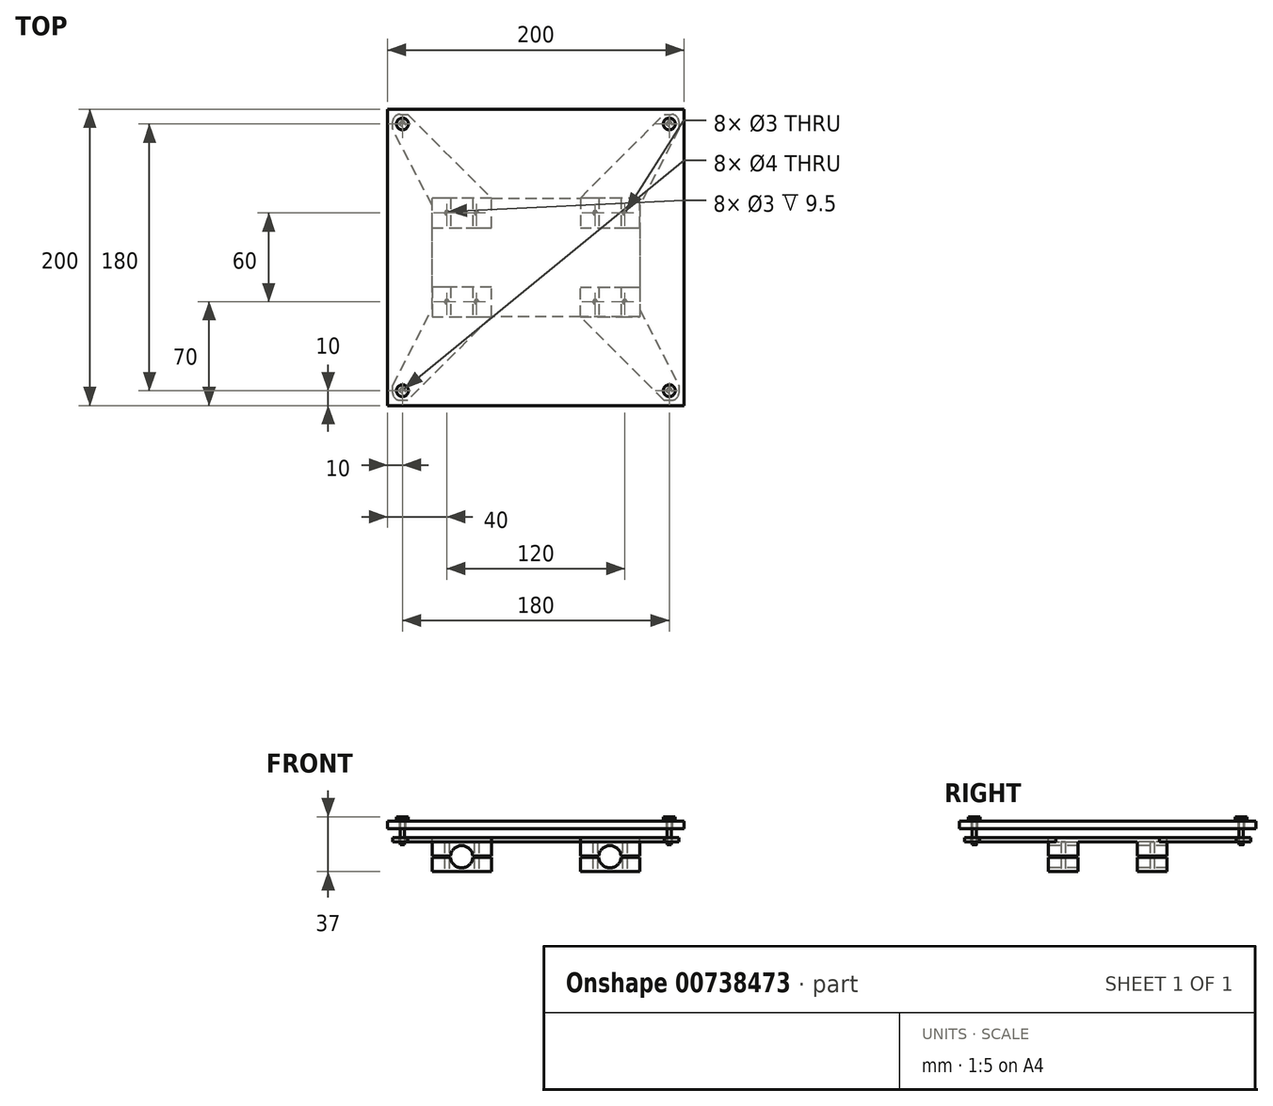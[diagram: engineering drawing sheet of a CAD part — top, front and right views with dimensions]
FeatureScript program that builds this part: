
annotation { "Feature Type Name" : "Feature", "Feature Type Description" : "" }
export const myFeature = defineFeature(function(context is Context, id is Id, definition is map)
    precondition{}
    {
        {
            var Q0;
            Q0=qCreatedBy(makeId("Top.planeOp"),FACE);
            var sketch = newSketch(context, id + "F0", { "sketchPlane" : qUnion([Q0])});
            skLineSegment(sketch, "E0.bottom", {"start": v(100, 100) * mm, "end": v(-100, 100) * mm});
            skLineSegment(sketch, "E0.top", {"start": v(100, -100) * mm, "end": v(-100, -100) * mm});
            skLineSegment(sketch, "E0.left", {"start": v(100, 100) * mm, "end": v(100, -100) * mm});
            skLineSegment(sketch, "E0.right", {"start": v(-100, 100) * mm, "end": v(-100, -100) * mm});
            skPoint(sketch, "E0.middle", {"position": v(0, 0) * mm});
            skLineSegment(sketch, "E1", {"start": v(-90, 100) * mm, "end": v(-90, -100) * mm, "construction": true});
            skLineSegment(sketch, "E2", {"start": v(-90, -100) * mm, "end": v(-100, -90) * mm, "construction": true});
            skLineSegment(sketch, "E3", {"start": v(-100, -90) * mm, "end": v(100, -90) * mm, "construction": true});
            skLineSegment(sketch, "E4", {"start": v(100, -90) * mm, "end": v(90, -100) * mm, "construction": true});
            skLineSegment(sketch, "E5", {"start": v(90, -100) * mm, "end": v(90, 100) * mm, "construction": true});
            skLineSegment(sketch, "E6", {"start": v(90, 100) * mm, "end": v(100, 90) * mm, "construction": true});
            skLineSegment(sketch, "E7", {"start": v(100, 90) * mm, "end": v(-100, 90) * mm, "construction": true});
            skLineSegment(sketch, "E8", {"start": v(-100, 90) * mm, "end": v(-90, 100) * mm, "construction": true});
            skCircle(sketch, "E9", {"center": v(-90, 90) * mm, "radius": 2 * mm});
            skCircle(sketch, "E10", {"center": v(90, 90) * mm, "radius": 2 * mm});
            skCircle(sketch, "E11", {"center": v(90, -90) * mm, "radius": 2 * mm});
            skCircle(sketch, "E12", {"center": v(-90, -90) * mm, "radius": 2 * mm});
            skCircle(sketch, "E13", {"center": v(-90, -90) * mm, "radius": 1.5 * mm});
            skCircle(sketch, "E14", {"center": v(-90, 90) * mm, "radius": 1.5 * mm});
            skCircle(sketch, "E15", {"center": v(90, 90) * mm, "radius": 1.5 * mm});
            skCircle(sketch, "E16", {"center": v(90, -90) * mm, "radius": 1.5 * mm});
            skSolve(sketch);
        }
        {
            var Q0;
            Q0=makeQuery(id+"F0.imprint","IMPRINT",FACE,{"disambiguationData":[TD([[makeQuery(id+"F0.imprint","IMPRINT",EDGE,{"derivedFrom":sQuery(id+"F0.wireOp",EDGE,"E0.bottom")}),1.0]])]});
            extrude(context, id + "F1", {"entities" : qUnion([Q0]), "depth" : 5 * mm, "offsetDistance" : 25 * mm});
        }
        {
            var Q0;
            Q0=makeQuery(id+"F0.imprint","IMPRINT",FACE,{"disambiguationData":[TD([[makeQuery(id+"F0.imprint","IMPRINT",EDGE,{"derivedFrom":sQuery(id+"F0.wireOp",EDGE,"E14")}),1.0]])]});
            var Q1;
            Q1=makeQuery(id+"F0.imprint","IMPRINT",FACE,{"disambiguationData":[TD([[makeQuery(id+"F0.imprint","IMPRINT",EDGE,{"derivedFrom":sQuery(id+"F0.wireOp",EDGE,"E16")}),1.0]])]});
            var Q2;
            Q2=makeQuery(id+"F0.imprint","IMPRINT",FACE,{"disambiguationData":[TD([[makeQuery(id+"F0.imprint","IMPRINT",EDGE,{"derivedFrom":sQuery(id+"F0.wireOp",EDGE,"E13")}),1.0]])]});
            var Q3;
            Q3=makeQuery(id+"F0.imprint","IMPRINT",FACE,{"disambiguationData":[TD([[makeQuery(id+"F0.imprint","IMPRINT",EDGE,{"derivedFrom":sQuery(id+"F0.wireOp",EDGE,"E15")}),1.0]])]});
            extrude(context, id + "F2", {"entities" : qUnion([Q0, Q1, Q2, Q3]), "endBound" : BoundingType.SYMMETRIC, "depth" : 12 * mm, "offsetDistance" : 25 * mm});
        }
        {
            var Q0;
            Q0=makeQuery(id+"F2.opExtrude","CAP_FACE",FACE,{"disambiguationData":[OSD([sQuery(id+"F0.wireOp",EDGE,"E16")])],"isStart":false});
            var sketch = newSketch(context, id + "F3", { "sketchPlane" : qUnion([Q0])});
            skCircle(sketch, "E17", {"center": v(90, -90) * mm, "radius": 4 * mm});
            skSolve(sketch);
        }
        {
            var Q0;
            Q0=makeQuery(id+"F3.imprint","IMPRINT",FACE,{"disambiguationData":[TD([[makeQuery(id+"F3.imprint","IMPRINT",EDGE,{"derivedFrom":sQuery(id+"F3.wireOp",EDGE,"E17")}),1.0]])]});
            var Q1;
            Q1=makeQuery(id+"F3.imprint","IMPRINT",FACE,{"disambiguationData":[TD([[makeQuery(id+"F3.imprint","IMPRINT",EDGE,{"derivedFrom":makeQuery(id+"F2.opExtrude","CAP_EDGE",EDGE,{"disambiguationData":[OSD([sQuery(id+"F0.wireOp",EDGE,"E16")])],"isStart":false})}),1.0]])]});
            extrude(context, id + "F4", {"entities" : qUnion([Q0, Q1]), "operationType" : NewBodyOperationType.ADD, "depth" : 2 * mm, "offsetDistance" : 25 * mm});
        }
        {
            var Q0;
            Q0=makeQuery(id+"F2.opExtrude","CAP_FACE",FACE,{"disambiguationData":[OSD([sQuery(id+"F0.wireOp",EDGE,"E13")])],"isStart":false});
            var sketch = newSketch(context, id + "F5", { "sketchPlane" : qUnion([Q0])});
            skCircle(sketch, "E18", {"center": v(-90, -90) * mm, "radius": 4 * mm});
            skSolve(sketch);
        }
        {
            var Q0;
            Q0=makeQuery(id+"F5.imprint","IMPRINT",FACE,{"disambiguationData":[TD([[makeQuery(id+"F5.imprint","IMPRINT",EDGE,{"derivedFrom":sQuery(id+"F5.wireOp",EDGE,"E18")}),1.0]])]});
            var Q1;
            Q1=makeQuery(id+"F5.imprint","IMPRINT",FACE,{"disambiguationData":[TD([[makeQuery(id+"F5.imprint","IMPRINT",EDGE,{"derivedFrom":makeQuery(id+"F2.opExtrude","CAP_EDGE",EDGE,{"disambiguationData":[OSD([sQuery(id+"F0.wireOp",EDGE,"E13")])],"isStart":false})}),1.0]])]});
            extrude(context, id + "F6", {"entities" : qUnion([Q0, Q1]), "operationType" : NewBodyOperationType.ADD, "depth" : 2 * mm, "offsetDistance" : 25 * mm});
        }
        {
            var Q0;
            Q0=makeQuery(id+"F2.opExtrude","CAP_FACE",FACE,{"disambiguationData":[OSD([sQuery(id+"F0.wireOp",EDGE,"E14")])],"isStart":false});
            var sketch = newSketch(context, id + "F7", { "sketchPlane" : qUnion([Q0])});
            skCircle(sketch, "E19", {"center": v(-90, 90) * mm, "radius": 4 * mm});
            skSolve(sketch);
        }
        {
            var Q0;
            Q0=makeQuery(id+"F7.imprint","IMPRINT",FACE,{"disambiguationData":[TD([[makeQuery(id+"F7.imprint","IMPRINT",EDGE,{"derivedFrom":sQuery(id+"F7.wireOp",EDGE,"E19")}),1.0]])]});
            var Q1;
            Q1=makeQuery(id+"F7.imprint","IMPRINT",FACE,{"disambiguationData":[TD([[makeQuery(id+"F7.imprint","IMPRINT",EDGE,{"derivedFrom":makeQuery(id+"F2.opExtrude","CAP_EDGE",EDGE,{"disambiguationData":[OSD([sQuery(id+"F0.wireOp",EDGE,"E14")])],"isStart":false})}),1.0]])]});
            extrude(context, id + "F8", {"entities" : qUnion([Q0, Q1]), "depth" : 2 * mm, "offsetDistance" : 25 * mm});
        }
        {
            var Q0;
            Q0=makeQuery(id+"F2.opExtrude","CAP_FACE",FACE,{"disambiguationData":[OSD([sQuery(id+"F0.wireOp",EDGE,"E15")])],"isStart":false});
            var sketch = newSketch(context, id + "F9", { "sketchPlane" : qUnion([Q0])});
            skCircle(sketch, "E20", {"center": v(90, 90) * mm, "radius": 4 * mm});
            skSolve(sketch);
        }
        {
            var Q0;
            Q0=makeQuery(id+"F9.imprint","IMPRINT",FACE,{"disambiguationData":[TD([[makeQuery(id+"F9.imprint","IMPRINT",EDGE,{"derivedFrom":sQuery(id+"F9.wireOp",EDGE,"E20")}),1.0]])]});
            var Q1;
            Q1=makeQuery(id+"F9.imprint","IMPRINT",FACE,{"disambiguationData":[TD([[makeQuery(id+"F9.imprint","IMPRINT",EDGE,{"derivedFrom":makeQuery(id+"F2.opExtrude","CAP_EDGE",EDGE,{"disambiguationData":[OSD([sQuery(id+"F0.wireOp",EDGE,"E15")])],"isStart":false})}),1.0]])]});
            extrude(context, id + "F10", {"entities" : qUnion([Q0, Q1]), "operationType" : NewBodyOperationType.ADD, "depth" : 2 * mm, "offsetDistance" : 25 * mm});
        }
        {
            var Q0;
            Q0=makeQuery(id+"F2.opExtrude","CAP_FACE",FACE,{"disambiguationData":[OSD([sQuery(id+"F0.wireOp",EDGE,"E16")])],"isStart":true});
            var sketch = newSketch(context, id + "F11", { "sketchPlane" : qUnion([Q0])});
            skLineSegment(sketch, "E21", {"start": v(-96.5, 96.5) * mm, "end": v(-96.5, 86.5) * mm});
            skLineSegment(sketch, "E22", {"start": v(-96.5, 86.5) * mm, "end": v(-70, 35) * mm});
            skLineSegment(sketch, "E23", {"start": v(-70, 35) * mm, "end": v(-70, -35) * mm});
            skLineSegment(sketch, "E24", {"start": v(-70, -35) * mm, "end": v(-96.5, -86.5) * mm});
            skLineSegment(sketch, "E25", {"start": v(-96.5, -86.5) * mm, "end": v(-96.5, -96.5) * mm});
            skLineSegment(sketch, "E26", {"start": v(-96.5, -96.5) * mm, "end": v(-86.5, -96.5) * mm});
            skLineSegment(sketch, "E27", {"start": v(-86.5, -96.5) * mm, "end": v(-30, -40) * mm});
            skLineSegment(sketch, "E28", {"start": v(-30, -40) * mm, "end": v(30, -40) * mm});
            skLineSegment(sketch, "E29", {"start": v(30, -40) * mm, "end": v(86.5, -96.5) * mm});
            skLineSegment(sketch, "E30", {"start": v(86.5, -96.5) * mm, "end": v(96.5, -96.5) * mm});
            skLineSegment(sketch, "E31", {"start": v(96.5, -96.5) * mm, "end": v(96.5, -86.5) * mm});
            skLineSegment(sketch, "E32", {"start": v(96.5, -86.5) * mm, "end": v(70, -35) * mm});
            skLineSegment(sketch, "E33", {"start": v(70, -35) * mm, "end": v(70, 35) * mm});
            skLineSegment(sketch, "E34", {"start": v(70, 35) * mm, "end": v(96.5, 86.5) * mm});
            skLineSegment(sketch, "E35", {"start": v(96.5, 86.5) * mm, "end": v(96.5, 96.5) * mm});
            skLineSegment(sketch, "E36", {"start": v(96.5, 96.5) * mm, "end": v(86.5, 96.5) * mm});
            skLineSegment(sketch, "E37", {"start": v(86.5, 96.5) * mm, "end": v(30, 40) * mm});
            skLineSegment(sketch, "E38", {"start": v(30, 40) * mm, "end": v(-30, 40) * mm});
            skLineSegment(sketch, "E39", {"start": v(-30, 40) * mm, "end": v(-86.5, 96.5) * mm});
            skLineSegment(sketch, "E40", {"start": v(-86.5, 96.5) * mm, "end": v(-96.5, 96.5) * mm});
            skCircle(sketch, "E41", {"center": v(90, 90) * mm, "radius": 2 * mm});
            skCircle(sketch, "E42", {"center": v(-90, 90) * mm, "radius": 2 * mm});
            skCircle(sketch, "E43", {"center": v(-90, -90) * mm, "radius": 2 * mm});
            skCircle(sketch, "E44", {"center": v(90, -90) * mm, "radius": 2 * mm});
            skSolve(sketch);
        }
        {
            var Q0;
            Q0=makeQuery(id+"F11.imprint","IMPRINT",FACE,{"disambiguationData":[TD([[makeQuery(id+"F11.imprint","IMPRINT",EDGE,{"derivedFrom":sQuery(id+"F11.wireOp",EDGE,"E21")}),1.0]])]});
            extrude(context, id + "F12", {"entities" : qUnion([Q0]), "depth" : 3 * mm, "offsetDistance" : 25 * mm});
        }
        {
            var Q0;
            Q0=makeQuery(id+"F2.opExtrude","CAP_FACE",FACE,{"disambiguationData":[OSD([sQuery(id+"F0.wireOp",EDGE,"E13")])],"isStart":true});
            extrude(context, id + "F13", {"entities" : qUnion([Q0]), "operationType" : NewBodyOperationType.ADD, "depth" : 5 * mm, "offsetDistance" : 25 * mm});
        }
        {
            var Q0;
            Q0=makeQuery(id+"F2.opExtrude","CAP_FACE",FACE,{"disambiguationData":[OSD([sQuery(id+"F0.wireOp",EDGE,"E16")])],"isStart":true});
            extrude(context, id + "F14", {"entities" : qUnion([Q0]), "operationType" : NewBodyOperationType.ADD, "depth" : 5 * mm, "offsetDistance" : 25 * mm});
        }
        {
            var Q0;
            Q0=makeQuery(id+"F2.opExtrude","CAP_FACE",FACE,{"disambiguationData":[OSD([sQuery(id+"F0.wireOp",EDGE,"E15")])],"isStart":true});
            extrude(context, id + "F15", {"entities" : qUnion([Q0]), "operationType" : NewBodyOperationType.ADD, "depth" : 5 * mm, "offsetDistance" : 25 * mm});
        }
        {
            var Q0;
            Q0=makeQuery(id+"F2.opExtrude","CAP_FACE",FACE,{"disambiguationData":[OSD([sQuery(id+"F0.wireOp",EDGE,"E14")])],"isStart":true});
            extrude(context, id + "F16", {"entities" : qUnion([Q0]), "operationType" : NewBodyOperationType.ADD, "depth" : 5 * mm, "offsetDistance" : 25 * mm});
        }
        {
            var Q0;
            Q0=makeQuery(id+"F12.opExtrude","SWEPT_EDGE",EDGE,{"disambiguationData":[OSD([sQuery(id+"F11.wireOp",EDGE,"E21"),sQuery(id+"F11.wireOp",EDGE,"E40")])]});
            fillet(context, id + "F17", {"entities" : qUnion([Q0]), "radius" : 5 * mm, "tangentPropagation" : true, "allowEdgeOverflow" : false});
        }
        {
            var Q0;
            Q0=makeQuery(id+"F12.opExtrude","SWEPT_EDGE",EDGE,{"disambiguationData":[OSD([sQuery(id+"F11.wireOp",EDGE,"E35"),sQuery(id+"F11.wireOp",EDGE,"E36")])]});
            fillet(context, id + "F18", {"entities" : qUnion([Q0]), "radius" : 5 * mm, "tangentPropagation" : true, "allowEdgeOverflow" : false});
        }
        {
            var Q0;
            Q0=makeQuery(id+"F12.opExtrude","SWEPT_EDGE",EDGE,{"disambiguationData":[OSD([sQuery(id+"F11.wireOp",EDGE,"E25"),sQuery(id+"F11.wireOp",EDGE,"E26")])]});
            fillet(context, id + "F19", {"entities" : qUnion([Q0]), "radius" : 5 * mm, "tangentPropagation" : true, "allowEdgeOverflow" : false});
        }
        {
            var Q0;
            Q0=makeQuery(id+"F12.opExtrude","SWEPT_EDGE",EDGE,{"disambiguationData":[OSD([sQuery(id+"F11.wireOp",EDGE,"E30"),sQuery(id+"F11.wireOp",EDGE,"E31")])]});
            fillet(context, id + "F20", {"entities" : qUnion([Q0]), "radius" : 5 * mm, "tangentPropagation" : true, "allowEdgeOverflow" : false});
        }
        {
            var Q0;
            Q0=makeQuery(id+"F12.opExtrude","CAP_FACE",FACE,{"disambiguationData":[OSD([sQuery(id+"F11.wireOp",EDGE,"E21"),sQuery(id+"F11.wireOp",EDGE,"E22"),sQuery(id+"F11.wireOp",EDGE,"E23"),sQuery(id+"F11.wireOp",EDGE,"E24"),sQuery(id+"F11.wireOp",EDGE,"E25"),sQuery(id+"F11.wireOp",EDGE,"E26"),sQuery(id+"F11.wireOp",EDGE,"E27"),sQuery(id+"F11.wireOp",EDGE,"E28"),sQuery(id+"F11.wireOp",EDGE,"E29"),sQuery(id+"F11.wireOp",EDGE,"E30"),sQuery(id+"F11.wireOp",EDGE,"E31"),sQuery(id+"F11.wireOp",EDGE,"E32"),sQuery(id+"F11.wireOp",EDGE,"E33"),sQuery(id+"F11.wireOp",EDGE,"E34"),sQuery(id+"F11.wireOp",EDGE,"E35"),sQuery(id+"F11.wireOp",EDGE,"E36"),sQuery(id+"F11.wireOp",EDGE,"E37"),sQuery(id+"F11.wireOp",EDGE,"E38"),sQuery(id+"F11.wireOp",EDGE,"E39"),sQuery(id+"F11.wireOp",EDGE,"E40"),sQuery(id+"F11.wireOp",EDGE,"E41"),sQuery(id+"F11.wireOp",EDGE,"E42"),sQuery(id+"F11.wireOp",EDGE,"E43"),sQuery(id+"F11.wireOp",EDGE,"E44")])],"isStart":false});
            var sketch = newSketch(context, id + "F21", { "sketchPlane" : qUnion([Q0])});
            skLineSegment(sketch, "E45", {"start": v(-30, 40) * mm, "end": v(-30, 20) * mm});
            skLineSegment(sketch, "E46", {"start": v(-30, 20) * mm, "end": v(-70, 20) * mm});
            skLineSegment(sketch, "E47", {"start": v(-70, 20) * mm, "end": v(-70, 40) * mm});
            skLineSegment(sketch, "E48", {"start": v(-70, 40) * mm, "end": v(-30, 40) * mm});
            skLineSegment(sketch, "E49", {"start": v(30, 40) * mm, "end": v(30, 20) * mm});
            skLineSegment(sketch, "E50", {"start": v(30, 20) * mm, "end": v(70, 20) * mm});
            skLineSegment(sketch, "E51", {"start": v(70, 20) * mm, "end": v(70, 40) * mm});
            skLineSegment(sketch, "E52", {"start": v(70, 40) * mm, "end": v(30, 40) * mm});
            skLineSegment(sketch, "E53", {"start": v(-70, -35) * mm, "end": v(-70, -20) * mm});
            skLineSegment(sketch, "E54", {"start": v(-70, -20) * mm, "end": v(-30, -20) * mm});
            skLineSegment(sketch, "E55", {"start": v(-30, -20) * mm, "end": v(-30, -40) * mm});
            skLineSegment(sketch, "E56", {"start": v(-30, -40) * mm, "end": v(-70, -40) * mm});
            skLineSegment(sketch, "E57", {"start": v(-70, -40) * mm, "end": v(-70, -35) * mm});
            skLineSegment(sketch, "E58", {"start": v(30, -40) * mm, "end": v(30, -20) * mm});
            skLineSegment(sketch, "E59", {"start": v(30, -20) * mm, "end": v(70, -20) * mm});
            skLineSegment(sketch, "E60", {"start": v(70, -20) * mm, "end": v(70, -40) * mm});
            skLineSegment(sketch, "E61", {"start": v(70, -40) * mm, "end": v(30, -40) * mm});
            skSolve(sketch);
        }
        {
            var Q0;
            Q0=makeQuery(id+"F21.imprint","IMPRINT",FACE,{"disambiguationData":[TD([[makeQuery(id+"F21.imprint","IMPRINT",EDGE,{"derivedFrom":sQuery(id+"F21.wireOp",EDGE,"E45")}),-1.0]])]});
            var Q1;
            Q1=makeQuery(id+"F21.imprint","IMPRINT",FACE,{"disambiguationData":[TD([[makeQuery(id+"F21.imprint","IMPRINT",EDGE,{"derivedFrom":sQuery(id+"F21.wireOp",EDGE,"E53")}),1.0]])]});
            var Q2;
            Q2=makeQuery(id+"F21.imprint","IMPRINT",FACE,{"disambiguationData":[TD([[makeQuery(id+"F21.imprint","IMPRINT",EDGE,{"derivedFrom":sQuery(id+"F21.wireOp",EDGE,"E58")}),-1.0]])]});
            var Q3;
            Q3=makeQuery(id+"F21.imprint","IMPRINT",FACE,{"disambiguationData":[TD([[makeQuery(id+"F21.imprint","IMPRINT",EDGE,{"derivedFrom":sQuery(id+"F21.wireOp",EDGE,"E49")}),1.0]])]});
            extrude(context, id + "F22", {"entities" : qUnion([Q0, Q1, Q2, Q3]), "operationType" : NewBodyOperationType.ADD, "depth" : 20 * mm, "offsetDistance" : 25 * mm});
        }
        {
            var Q0;
            Q0=makeQuery(id+"F22.opExtrude","SWEPT_FACE",FACE,{"disambiguationData":[OSD([sQuery(id+"F21.wireOp",EDGE,"E48")])]});
            var sketch = newSketch(context, id + "F23", { "sketchPlane" : qUnion([Q0])});
            skLineSegment(sketch, "E62", {"start": v(-70, -9) * mm, "end": v(-30, -29) * mm, "construction": true});
            skLineSegment(sketch, "E63", {"start": v(-30, -29) * mm, "end": v(-30, -9) * mm, "construction": true});
            skLineSegment(sketch, "E64", {"start": v(-30, -9) * mm, "end": v(-70, -29) * mm, "construction": true});
            skCircle(sketch, "E65", {"center": v(-50, -19) * mm, "radius": 7.5 * mm});
            skLineSegment(sketch, "E66", {"start": v(-30, -19) * mm, "end": v(-70, -19) * mm, "construction": true});
            skLineSegment(sketch, "E67", {"start": v(-70, -18.5) * mm, "end": v(-30, -18.5) * mm});
            skLineSegment(sketch, "E68", {"start": v(-70, -19.5) * mm, "end": v(-30, -19.5) * mm});
            skSolve(sketch);
        }
        {
            var Q0;
            {var subQ0=sQuery(id+"F23.wireOp",EDGE,"E67");var subQ1=sQuery(id+"F23.wireOp",EDGE,"E65");var subQ2=makeQuery(id+"F23.imprint","INTERSECT",VERTEX,{"disambiguationData":[OD(0.0)],"derivedFrom":[subQ1,subQ0]});Q0=makeQuery(id+"F23.imprint","IMPRINT",FACE,{"disambiguationData":[TD([[makeQuery(id+"F23.imprint","IMPRINT",EDGE,{"disambiguationData":[TD([[subQ2,-1.0]])],"derivedFrom":subQ1}),1.0]])]});}
            var Q1;
            {var subQ0=sQuery(id+"F23.wireOp",EDGE,"E67");var subQ1=sQuery(id+"F23.wireOp",EDGE,"E65");var subQ2=makeQuery(id+"F23.imprint","INTERSECT",VERTEX,{"disambiguationData":[OD(0.0)],"derivedFrom":[subQ1,subQ0]});Q1=makeQuery(id+"F23.imprint","IMPRINT",FACE,{"disambiguationData":[TD([[makeQuery(id+"F23.imprint","IMPRINT",EDGE,{"disambiguationData":[TD([[subQ2,1.0]])],"derivedFrom":subQ1}),1.0]])]});}
            var Q2;
            {var subQ0=sQuery(id+"F23.wireOp",EDGE,"E68");var subQ1=sQuery(id+"F23.wireOp",EDGE,"E65");var subQ2=makeQuery(id+"F23.imprint","INTERSECT",VERTEX,{"disambiguationData":[OD(0.0)],"derivedFrom":[subQ1,subQ0]});Q2=makeQuery(id+"F23.imprint","IMPRINT",FACE,{"disambiguationData":[TD([[makeQuery(id+"F23.imprint","IMPRINT",EDGE,{"disambiguationData":[TD([[subQ2,-1.0]])],"derivedFrom":subQ1}),1.0]])]});}
            var Q3;
            {var subQ0=sQuery(id+"F23.wireOp",EDGE,"E67");var subQ1=sQuery(id+"F23.wireOp",EDGE,"E65");var subQ2=makeQuery(id+"F23.imprint","INTERSECT",VERTEX,{"disambiguationData":[OD(0.0)],"derivedFrom":[subQ1,subQ0]});Q3=makeQuery(id+"F23.imprint","IMPRINT",FACE,{"disambiguationData":[TD([[makeQuery(id+"F23.imprint","IMPRINT",EDGE,{"disambiguationData":[TD([[subQ2,-1.0]])],"derivedFrom":subQ1}),-1.0]])]});}
            var Q4;
            {var subQ0=sQuery(id+"F23.wireOp",EDGE,"E67");var subQ1=sQuery(id+"F23.wireOp",EDGE,"E65");var subQ2=makeQuery(id+"F23.imprint","INTERSECT",VERTEX,{"disambiguationData":[OD(1.0)],"derivedFrom":[subQ1,subQ0]});Q4=makeQuery(id+"F23.imprint","IMPRINT",FACE,{"disambiguationData":[TD([[makeQuery(id+"F23.imprint","IMPRINT",EDGE,{"disambiguationData":[TD([[subQ2,1.0]])],"derivedFrom":subQ1}),-1.0]])]});}
            extrude(context, id + "F24", {"entities" : qUnion([Q0, Q1, Q2, Q3, Q4]), "operationType" : NewBodyOperationType.REMOVE, "oppositeDirection" : true, "depth" : 90 * mm, "offsetDistance" : 25 * mm});
        }
        {
            var Q0;
            Q0=makeQuery(id+"F22.opExtrude","SWEPT_FACE",FACE,{"disambiguationData":[OSD([sQuery(id+"F21.wireOp",EDGE,"E52")])]});
            var sketch = newSketch(context, id + "F25", { "sketchPlane" : qUnion([Q0])});
            skLineSegment(sketch, "E69", {"start": v(30, -9) * mm, "end": v(70, -29) * mm, "construction": true});
            skLineSegment(sketch, "E70", {"start": v(70, -29) * mm, "end": v(70, -9) * mm, "construction": true});
            skLineSegment(sketch, "E71", {"start": v(70, -9) * mm, "end": v(30, -29) * mm, "construction": true});
            skLineSegment(sketch, "E72", {"start": v(30, -29) * mm, "end": v(30, -19) * mm, "construction": true});
            skLineSegment(sketch, "E73", {"start": v(30, -19) * mm, "end": v(70, -19) * mm, "construction": true});
            skLineSegment(sketch, "E74", {"start": v(30, -18.5) * mm, "end": v(70, -18.5) * mm});
            skLineSegment(sketch, "E75", {"start": v(30, -19.5) * mm, "end": v(70, -19.5) * mm});
            skCircle(sketch, "E76", {"center": v(50, -19) * mm, "radius": 7.5 * mm});
            skSolve(sketch);
        }
        {
            var Q0;
            {var subQ0=sQuery(id+"F25.wireOp",EDGE,"E76");var subQ1=sQuery(id+"F25.wireOp",EDGE,"E74");var subQ2=makeQuery(id+"F25.imprint","INTERSECT",VERTEX,{"disambiguationData":[OD(0.0)],"derivedFrom":[subQ1,subQ0]});Q0=makeQuery(id+"F25.imprint","IMPRINT",FACE,{"disambiguationData":[TD([[makeQuery(id+"F25.imprint","IMPRINT",EDGE,{"disambiguationData":[TD([[subQ2,-1.0]])],"derivedFrom":subQ1}),1.0]])]});}
            var Q1;
            {var subQ0=sQuery(id+"F25.wireOp",EDGE,"E76");var subQ1=sQuery(id+"F25.wireOp",EDGE,"E75");var subQ2=makeQuery(id+"F25.imprint","INTERSECT",VERTEX,{"disambiguationData":[OD(0.0)],"derivedFrom":[subQ1,subQ0]});Q1=makeQuery(id+"F25.imprint","IMPRINT",FACE,{"disambiguationData":[TD([[makeQuery(id+"F25.imprint","IMPRINT",EDGE,{"disambiguationData":[TD([[subQ2,-1.0]])],"derivedFrom":subQ1}),-1.0]])]});}
            var Q2;
            {var subQ0=sQuery(id+"F25.wireOp",EDGE,"E74");var subQ3=sQuery(id+"F25.wireOp",EDGE,"E76");var subQ4=makeQuery(id+"F25.imprint","INTERSECT",VERTEX,{"disambiguationData":[OD(0.0)],"derivedFrom":[subQ0,subQ3]});Q2=makeQuery(id+"F25.imprint","IMPRINT",FACE,{"disambiguationData":[TD([[makeQuery(id+"F25.imprint","IMPRINT",EDGE,{"disambiguationData":[TD([[subQ4,-1.0]])],"derivedFrom":subQ3}),-1.0]])]});}
            var Q3;
            {var subQ0=sQuery(id+"F25.wireOp",EDGE,"E76");var subQ1=sQuery(id+"F25.wireOp",EDGE,"E74");var subQ2=makeQuery(id+"F25.imprint","INTERSECT",VERTEX,{"disambiguationData":[OD(0.0)],"derivedFrom":[subQ1,subQ0]});Q3=makeQuery(id+"F25.imprint","IMPRINT",FACE,{"disambiguationData":[TD([[makeQuery(id+"F25.imprint","IMPRINT",EDGE,{"disambiguationData":[TD([[subQ2,-1.0]])],"derivedFrom":subQ1}),-1.0]])]});}
            var Q4;
            {var subQ0=sQuery(id+"F25.wireOp",EDGE,"E74");var subQ3=sQuery(id+"F25.wireOp",EDGE,"E76");var subQ4=makeQuery(id+"F25.imprint","INTERSECT",VERTEX,{"disambiguationData":[OD(1.0)],"derivedFrom":[subQ0,subQ3]});Q4=makeQuery(id+"F25.imprint","IMPRINT",FACE,{"disambiguationData":[TD([[makeQuery(id+"F25.imprint","IMPRINT",EDGE,{"disambiguationData":[TD([[subQ4,1.0]])],"derivedFrom":subQ3}),-1.0]])]});}
            extrude(context, id + "F26", {"entities" : qUnion([Q0, Q1, Q2, Q3, Q4]), "operationType" : NewBodyOperationType.REMOVE, "oppositeDirection" : true, "depth" : 90 * mm, "offsetDistance" : 25 * mm});
        }
        {
            var Q0;
            Q0=makeQuery(id+"F22.opExtrude","CAP_FACE",FACE,{"disambiguationData":[OSD([sQuery(id+"F21.wireOp",EDGE,"E49"),sQuery(id+"F21.wireOp",EDGE,"E50"),sQuery(id+"F21.wireOp",EDGE,"E51"),sQuery(id+"F21.wireOp",EDGE,"E52")])],"isStart":false});
            var sketch = newSketch(context, id + "F27", { "sketchPlane" : qUnion([Q0])});
            skLineSegment(sketch, "E77", {"start": v(30, 40) * mm, "end": v(50, 20) * mm, "construction": true});
            skLineSegment(sketch, "E78", {"start": v(50, 20) * mm, "end": v(70, 40) * mm, "construction": true});
            skLineSegment(sketch, "E79", {"start": v(70, 40) * mm, "end": v(70, 20) * mm, "construction": true});
            skLineSegment(sketch, "E80", {"start": v(70, 20) * mm, "end": v(50, 40) * mm, "construction": true});
            skLineSegment(sketch, "E81", {"start": v(50, 40) * mm, "end": v(30, 20) * mm, "construction": true});
            skCircle(sketch, "E82", {"center": v(40, 30) * mm, "radius": 1.5 * mm});
            skCircle(sketch, "E83", {"center": v(60, 30) * mm, "radius": 1.5 * mm});
            skSolve(sketch);
        }
        {
            var Q0;
            Q0=makeQuery(id+"F27.imprint","IMPRINT",FACE,{"disambiguationData":[TD([[makeQuery(id+"F27.imprint","IMPRINT",EDGE,{"derivedFrom":sQuery(id+"F27.wireOp",EDGE,"E82")}),1.0]])]});
            var Q1;
            Q1=makeQuery(id+"F27.imprint","IMPRINT",FACE,{"disambiguationData":[TD([[makeQuery(id+"F27.imprint","IMPRINT",EDGE,{"derivedFrom":sQuery(id+"F27.wireOp",EDGE,"E83")}),1.0]])]});
            extrude(context, id + "F28", {"entities" : qUnion([Q0, Q1]), "operationType" : NewBodyOperationType.REMOVE, "oppositeDirection" : true, "depth" : 20 * mm, "offsetDistance" : 25 * mm});
        }
        {
            var Q0;
            Q0=makeQuery(id+"F22.opExtrude","CAP_FACE",FACE,{"disambiguationData":[OSD([sQuery(id+"F21.wireOp",EDGE,"E58"),sQuery(id+"F21.wireOp",EDGE,"E59"),sQuery(id+"F21.wireOp",EDGE,"E60"),sQuery(id+"F21.wireOp",EDGE,"E61")])],"isStart":false});
            var sketch = newSketch(context, id + "F29", { "sketchPlane" : qUnion([Q0])});
            skLineSegment(sketch, "E84", {"start": v(30, -20) * mm, "end": v(50, -40) * mm, "construction": true});
            skLineSegment(sketch, "E85", {"start": v(50, -40) * mm, "end": v(70, -20) * mm, "construction": true});
            skLineSegment(sketch, "E86", {"start": v(70, -20) * mm, "end": v(70, -40) * mm, "construction": true});
            skLineSegment(sketch, "E87", {"start": v(70, -40) * mm, "end": v(50, -20) * mm, "construction": true});
            skLineSegment(sketch, "E88", {"start": v(50, -20) * mm, "end": v(30, -40) * mm, "construction": true});
            skCircle(sketch, "E89", {"center": v(40, -30) * mm, "radius": 1.5 * mm});
            skCircle(sketch, "E90", {"center": v(60, -30) * mm, "radius": 1.5 * mm});
            skSolve(sketch);
        }
        {
            var Q0;
            Q0=makeQuery(id+"F29.imprint","IMPRINT",FACE,{"disambiguationData":[TD([[makeQuery(id+"F29.imprint","IMPRINT",EDGE,{"derivedFrom":sQuery(id+"F29.wireOp",EDGE,"E89")}),1.0]])]});
            var Q1;
            Q1=makeQuery(id+"F29.imprint","IMPRINT",FACE,{"disambiguationData":[TD([[makeQuery(id+"F29.imprint","IMPRINT",EDGE,{"derivedFrom":sQuery(id+"F29.wireOp",EDGE,"E90")}),1.0]])]});
            extrude(context, id + "F30", {"entities" : qUnion([Q0, Q1]), "operationType" : NewBodyOperationType.REMOVE, "oppositeDirection" : true, "depth" : 20 * mm, "offsetDistance" : 25 * mm});
        }
        {
            var Q0;
            Q0=makeQuery(id+"F22.opExtrude","CAP_FACE",FACE,{"disambiguationData":[OSD([sQuery(id+"F21.wireOp",EDGE,"E53"),sQuery(id+"F21.wireOp",EDGE,"E54"),sQuery(id+"F21.wireOp",EDGE,"E55"),sQuery(id+"F21.wireOp",EDGE,"E56"),sQuery(id+"F21.wireOp",EDGE,"E57")])],"isStart":false});
            var sketch = newSketch(context, id + "F31", { "sketchPlane" : qUnion([Q0])});
            skLineSegment(sketch, "E91", {"start": v(-70, -20) * mm, "end": v(-50, -40) * mm, "construction": true});
            skLineSegment(sketch, "E92", {"start": v(-50, -40) * mm, "end": v(-30, -20) * mm, "construction": true});
            skLineSegment(sketch, "E93", {"start": v(-30, -20) * mm, "end": v(-30, -40) * mm});
            skLineSegment(sketch, "E94", {"start": v(-30, -40) * mm, "end": v(-50, -20) * mm, "construction": true});
            skLineSegment(sketch, "E95", {"start": v(-50, -20) * mm, "end": v(-70, -40) * mm, "construction": true});
            skCircle(sketch, "E96", {"center": v(-60, -30) * mm, "radius": 1.5 * mm});
            skCircle(sketch, "E97", {"center": v(-40, -30) * mm, "radius": 1.5 * mm});
            skSolve(sketch);
        }
        {
            var Q0;
            Q0=makeQuery(id+"F31.imprint","IMPRINT",FACE,{"disambiguationData":[TD([[makeQuery(id+"F31.imprint","IMPRINT",EDGE,{"derivedFrom":sQuery(id+"F31.wireOp",EDGE,"E96")}),1.0]])]});
            var Q1;
            Q1=makeQuery(id+"F31.imprint","IMPRINT",FACE,{"disambiguationData":[TD([[makeQuery(id+"F31.imprint","IMPRINT",EDGE,{"derivedFrom":sQuery(id+"F31.wireOp",EDGE,"E97")}),1.0]])]});
            extrude(context, id + "F32", {"entities" : qUnion([Q0, Q1]), "operationType" : NewBodyOperationType.REMOVE, "oppositeDirection" : true, "depth" : 20 * mm, "offsetDistance" : 25 * mm});
        }
        {
            var Q0;
            Q0=makeQuery(id+"F22.opExtrude","CAP_FACE",FACE,{"disambiguationData":[OSD([sQuery(id+"F21.wireOp",EDGE,"E45"),sQuery(id+"F21.wireOp",EDGE,"E46"),sQuery(id+"F21.wireOp",EDGE,"E47"),sQuery(id+"F21.wireOp",EDGE,"E48")])],"isStart":false});
            var sketch = newSketch(context, id + "F33", { "sketchPlane" : qUnion([Q0])});
            skLineSegment(sketch, "E98", {"start": v(-70, 40) * mm, "end": v(-50, 20) * mm, "construction": true});
            skLineSegment(sketch, "E99", {"start": v(-50, 20) * mm, "end": v(-30, 40) * mm, "construction": true});
            skLineSegment(sketch, "E100", {"start": v(-30, 40) * mm, "end": v(-30, 20) * mm, "construction": true});
            skLineSegment(sketch, "E101", {"start": v(-30, 20) * mm, "end": v(-50, 40) * mm, "construction": true});
            skLineSegment(sketch, "E102", {"start": v(-50, 40) * mm, "end": v(-70, 20) * mm, "construction": true});
            skCircle(sketch, "E103", {"center": v(-60, 30) * mm, "radius": 1.5 * mm});
            skPoint(sketch, "E103.perimeterSnap0", {"position": v(-60, 30) * mm});
            skCircle(sketch, "E104", {"center": v(-40, 30) * mm, "radius": 1.5 * mm});
            skPoint(sketch, "E104.perimeterSnap0", {"position": v(-40, 30) * mm});
            skSolve(sketch);
        }
        {
            var Q0;
            Q0=makeQuery(id+"F33.imprint","IMPRINT",FACE,{"disambiguationData":[TD([[makeQuery(id+"F33.imprint","IMPRINT",EDGE,{"derivedFrom":sQuery(id+"F33.wireOp",EDGE,"E103")}),1.0]])]});
            var Q1;
            Q1=makeQuery(id+"F33.imprint","IMPRINT",FACE,{"disambiguationData":[TD([[makeQuery(id+"F33.imprint","IMPRINT",EDGE,{"derivedFrom":sQuery(id+"F33.wireOp",EDGE,"E104")}),1.0]])]});
            extrude(context, id + "F34", {"entities" : qUnion([Q0, Q1]), "operationType" : NewBodyOperationType.REMOVE, "oppositeDirection" : true, "depth" : 20 * mm, "offsetDistance" : 25 * mm});
        }
    });
